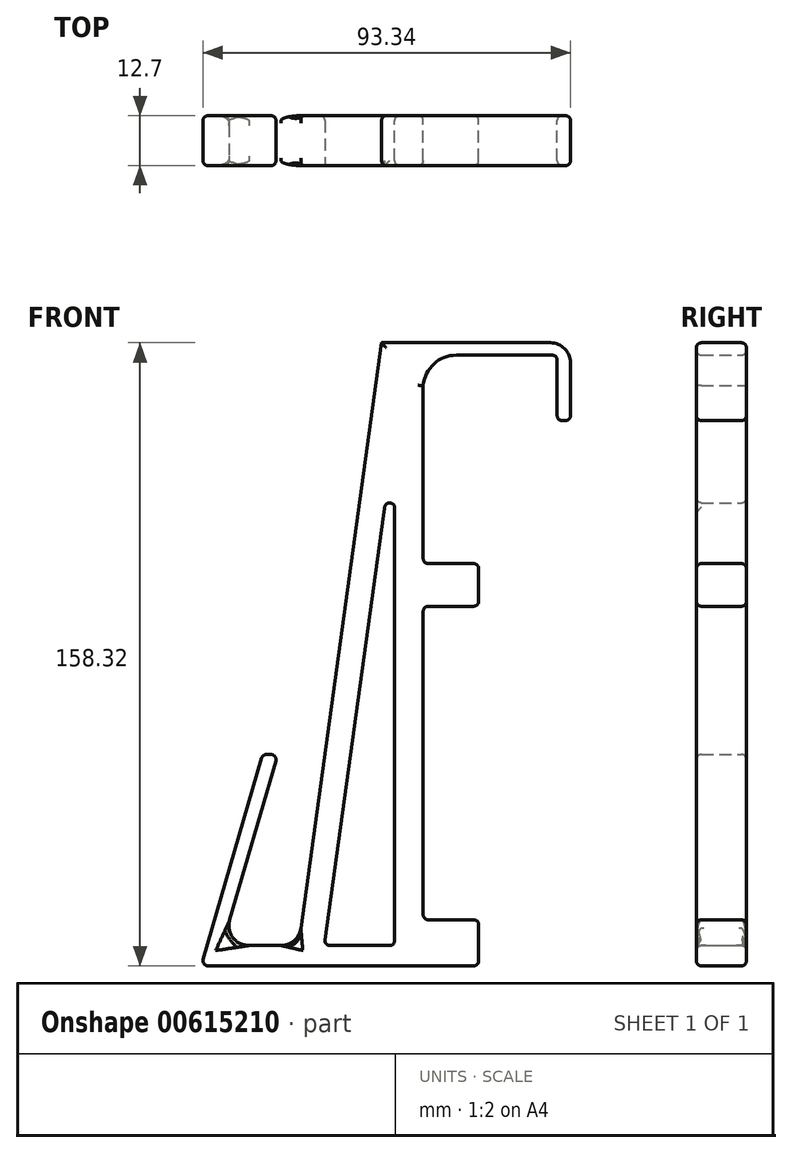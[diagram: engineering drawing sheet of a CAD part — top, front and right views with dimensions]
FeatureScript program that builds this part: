
annotation { "Feature Type Name" : "Feature", "Feature Type Description" : "" }
export const myFeature = defineFeature(function(context is Context, id is Id, definition is map)
    precondition{}
    {
        {
            var Q0;
            Q0=qCreatedBy(makeId("Front.planeOp"),FACE);
            var sketch = newSketch(context, id + "F0", { "sketchPlane" : qUnion([Q0])});
            skLineSegment(sketch, "E0", {"start": v(38.7, 133.36) * mm, "end": v(38.7, 150.01) * mm});
            skLineSegment(sketch, "E1", {"start": v(38.7, 150.01) * mm, "end": v(13.07, 150.01) * mm});
            skLineSegment(sketch, "E2", {"start": v(4.65, 142.3) * mm, "end": v(4.65, 97.04) * mm});
            skLineSegment(sketch, "E3", {"start": v(4.65, -5.16) * mm, "end": v(-51.7, -5.16) * mm});
            skLineSegment(sketch, "E4", {"start": v(-51.7, -5.16) * mm, "end": v(-36.14, 48.54) * mm});
            skLineSegment(sketch, "E5", {"start": v(-36.14, 48.54) * mm, "end": v(-32.33, 48.54) * mm});
            skLineSegment(sketch, "E6", {"start": v(-32.33, 48.54) * mm, "end": v(-46.39, 0) * mm});
            skLineSegment(sketch, "E7", {"start": v(-46.39, 0) * mm, "end": v(-27.04, 0) * mm});
            skLineSegment(sketch, "E8", {"start": v(-27.04, 0) * mm, "end": v(-6.11, 151.7) * mm});
            skLineSegment(sketch, "E9", {"start": v(-20.5, 0) * mm, "end": v(-2.6, 0) * mm});
            skPoint(sketch, "E10.start.orphan", {"position": v(0.23, 153.16) * mm});
            skLineSegment(sketch, "E11", {"start": v(-2.6, 129.72) * mm, "end": v(-20.5, 0) * mm});
            skLineSegment(sketch, "E12", {"start": v(4.65, 97.04) * mm, "end": v(18.75, 97.04) * mm});
            skLineSegment(sketch, "E13", {"start": v(18.75, 97.04) * mm, "end": v(18.75, 86.2) * mm});
            skLineSegment(sketch, "E14", {"start": v(18.75, 86.2) * mm, "end": v(4.65, 86.2) * mm});
            skLineSegment(sketch, "E15.trimOffspring", {"start": v(4.65, 86.2) * mm, "end": v(4.65, 6.56) * mm});
            skPoint(sketch, "E16.orphan", {"position": v(-5.91, 153.16) * mm});
            skLineSegment(sketch, "E17", {"start": v(4.65, 6.56) * mm, "end": v(18.75, 6.56) * mm});
            skLineSegment(sketch, "E18", {"start": v(18.75, 6.56) * mm, "end": v(18.75, -5.16) * mm});
            skLineSegment(sketch, "E19", {"start": v(18.75, -5.16) * mm, "end": v(4.65, -5.16) * mm});
            skLineSegment(sketch, "E20", {"start": v(38.7, 133.36) * mm, "end": v(42.06, 133.36) * mm});
            skLineSegment(sketch, "E21", {"start": v(42.06, 133.36) * mm, "end": v(42.06, 153.16) * mm});
            skLineSegment(sketch, "E22", {"start": v(42.06, 153.16) * mm, "end": v(-5.91, 153.16) * mm});
            skLineSegment(sketch, "E23", {"start": v(-6.11, 151.7) * mm, "end": v(-5.91, 153.16) * mm});
            skPoint(sketch, "E24.orphan", {"position": v(0, 129.72) * mm});
            skLineSegment(sketch, "E25", {"start": v(-2.6, 129.72) * mm, "end": v(-2.6, 0) * mm});
            skPoint(sketch, "E26.start.orphan", {"position": v(-1.3, 129.72) * mm});
            skPoint(sketch, "E27.centerSnap0", {"position": v(38.7, 141.69) * mm});
            skPoint(sketch, "E28", {"position": v(4.65, 142.3) * mm});
            skPoint(sketch, "E29", {"position": v(13.07, 150.01) * mm});
            skArc(sketch, "E30", {"start": v(13.07, 150.01) * mm, "mid": v(7.38, 147.77) * mm, "end": v(4.65, 142.3) * mm});
            skSolve(sketch);
        }
        {
            var Q0;
            Q0=makeQuery(id+"F0.imprint","IMPRINT",FACE,{"disambiguationData":[TD([[makeQuery(id+"F0.imprint","IMPRINT",EDGE,{"derivedFrom":sQuery(id+"F0.wireOp",EDGE,"KnBHMKyh-VmdD-H7sI-4YRO-vwrzje6zqPXn")}),-1.0]])]});
            var Q1;
            {var subQ2=sQuery(id+"F0.wireOp",EDGE,"E0");Q1=makeQuery(id+"F0.imprint","IMPRINT",FACE,{"disambiguationData":[TD([[makeQuery(id+"F0.imprint","IMPRINT",EDGE,{"derivedFrom":subQ2}),-1.0]])]});}
            extrude(context, id + "F1", {"entities" : qUnion([Q0, Q1]), "depth" : 12.7 * mm, "offsetDistance" : 25.4 * mm});
        }
        {
            var Q0;
            Q0=makeQuery(id+"F1.opExtrude","SWEPT_EDGE",EDGE,{"disambiguationData":[OSD([sQuery(id+"F0.wireOp",EDGE,"E11"),sQuery(id+"F0.wireOp",EDGE,"Bk6zNjHY-LAlG-lBTS-agNk-ghVCI7C8jAzF")])]});
            var Q1;
            Q1=makeQuery(id+"F1.opExtrude","CAP_EDGE",EDGE,{"disambiguationData":[OSD([sQuery(id+"F0.wireOp",EDGE,"Bk6zNjHY-LAlG-lBTS-agNk-ghVCI7C8jAzF")])],"isStart":false});
            var Q2;
            Q2=makeQuery(id+"F1.opExtrude","CAP_EDGE",EDGE,{"disambiguationData":[OSD([sQuery(id+"F0.wireOp",EDGE,"E26")])],"isStart":false});
            var Q3;
            Q3=makeQuery(id+"F1.opExtrude","SWEPT_EDGE",EDGE,{"disambiguationData":[OSD([sQuery(id+"F0.wireOp",EDGE,"Bk6zNjHY-LAlG-lBTS-agNk-ghVCI7C8jAzF"),sQuery(id+"F0.wireOp",EDGE,"E26")])]});
            var Q4;
            Q4=makeQuery(id+"F1.opExtrude","CAP_EDGE",EDGE,{"disambiguationData":[OSD([sQuery(id+"F0.wireOp",EDGE,"E25")])],"isStart":false});
            var Q5;
            Q5=makeQuery(id+"F1.opExtrude","CAP_EDGE",EDGE,{"disambiguationData":[OSD([sQuery(id+"F0.wireOp",EDGE,"E2")])],"isStart":false});
            var Q6;
            Q6=makeQuery(id+"F1.opExtrude","CAP_EDGE",EDGE,{"disambiguationData":[OSD([sQuery(id+"F0.wireOp",EDGE,"E2")])],"isStart":true});
            var Q7;
            Q7=makeQuery(id+"F1.opExtrude","CAP_EDGE",EDGE,{"disambiguationData":[OSD([sQuery(id+"F0.wireOp",EDGE,"E1")])],"isStart":false});
            var Q8;
            Q8=makeQuery(id+"F1.opExtrude","CAP_EDGE",EDGE,{"disambiguationData":[OSD([sQuery(id+"F0.wireOp",EDGE,"E21")])],"isStart":false});
            var Q9;
            Q9=makeQuery(id+"F1.opExtrude","CAP_EDGE",EDGE,{"disambiguationData":[OSD([sQuery(id+"F0.wireOp",EDGE,"E20")])],"isStart":false});
            var Q10;
            Q10=makeQuery(id+"F1.opExtrude","SWEPT_EDGE",EDGE,{"disambiguationData":[OSD([sQuery(id+"F0.wireOp",EDGE,"E20"),sQuery(id+"F0.wireOp",EDGE,"E21")])]});
            var Q11;
            Q11=makeQuery(id+"F1.opExtrude","SWEPT_EDGE",EDGE,{"disambiguationData":[OSD([sQuery(id+"F0.wireOp",EDGE,"E0"),sQuery(id+"F0.wireOp",EDGE,"E20")])]});
            var Q12;
            Q12=makeQuery(id+"F1.opExtrude","CAP_EDGE",EDGE,{"disambiguationData":[OSD([sQuery(id+"F0.wireOp",EDGE,"E1")])],"isStart":true});
            var Q13;
            Q13=makeQuery(id+"F1.opExtrude","CAP_EDGE",EDGE,{"disambiguationData":[OSD([sQuery(id+"F0.wireOp",EDGE,"E22")])],"isStart":false});
            var Q14;
            Q14=makeQuery(id+"F1.opExtrude","CAP_FACE",FACE,{"disambiguationData":[OSD([sQuery(id+"F0.wireOp",EDGE,"E0"),sQuery(id+"F0.wireOp",EDGE,"E1"),sQuery(id+"F0.wireOp",EDGE,"E2"),sQuery(id+"F0.wireOp",EDGE,"E3"),sQuery(id+"F0.wireOp",EDGE,"E4"),sQuery(id+"F0.wireOp",EDGE,"E5"),sQuery(id+"F0.wireOp",EDGE,"E6"),sQuery(id+"F0.wireOp",EDGE,"E7"),sQuery(id+"F0.wireOp",EDGE,"E8"),sQuery(id+"F0.wireOp",EDGE,"E9"),sQuery(id+"F0.wireOp",EDGE,"E11"),sQuery(id+"F0.wireOp",EDGE,"E12"),sQuery(id+"F0.wireOp",EDGE,"E13"),sQuery(id+"F0.wireOp",EDGE,"E14"),sQuery(id+"F0.wireOp",EDGE,"E15.trimOffspring"),sQuery(id+"F0.wireOp",EDGE,"E17"),sQuery(id+"F0.wireOp",EDGE,"E18"),sQuery(id+"F0.wireOp",EDGE,"E19"),sQuery(id+"F0.wireOp",EDGE,"E20"),sQuery(id+"F0.wireOp",EDGE,"E21"),sQuery(id+"F0.wireOp",EDGE,"E22"),sQuery(id+"F0.wireOp",EDGE,"E23"),sQuery(id+"F0.wireOp",EDGE,"E25")])],"isStart":true});
            var Q15;
            Q15=makeQuery(id+"F1.opExtrude","SWEPT_EDGE",EDGE,{"disambiguationData":[OSD([sQuery(id+"F0.wireOp",EDGE,"E4"),sQuery(id+"F0.wireOp",EDGE,"E5")])]});
            var Q16;
            Q16=makeQuery(id+"F1.opExtrude","SWEPT_EDGE",EDGE,{"disambiguationData":[OSD([sQuery(id+"F0.wireOp",EDGE,"E5"),sQuery(id+"F0.wireOp",EDGE,"E6")])]});
            var Q17;
            Q17=makeQuery(id+"F1.opExtrude","CAP_EDGE",EDGE,{"disambiguationData":[OSD([sQuery(id+"F0.wireOp",EDGE,"E5")])],"isStart":false});
            var Q18;
            Q18=makeQuery(id+"F1.opExtrude","CAP_EDGE",EDGE,{"disambiguationData":[OSD([sQuery(id+"F0.wireOp",EDGE,"E6")])],"isStart":false});
            var Q19;
            Q19=makeQuery(id+"F1.opExtrude","CAP_EDGE",EDGE,{"disambiguationData":[OSD([sQuery(id+"F0.wireOp",EDGE,"E4")])],"isStart":false});
            var Q20;
            Q20=makeQuery(id+"F1.opExtrude","CAP_EDGE",EDGE,{"disambiguationData":[OSD([sQuery(id+"F0.wireOp",EDGE,"E8"),sQuery(id+"F0.wireOp",EDGE,"E23")])],"isStart":false});
            var Q21;
            Q21=makeQuery(id+"F1.opExtrude","SWEPT_EDGE",EDGE,{"disambiguationData":[OSD([sQuery(id+"F0.wireOp",EDGE,"E12"),sQuery(id+"F0.wireOp",EDGE,"E13")])]});
            var Q22;
            Q22=makeQuery(id+"F1.opExtrude","SWEPT_EDGE",EDGE,{"disambiguationData":[OSD([sQuery(id+"F0.wireOp",EDGE,"E13"),sQuery(id+"F0.wireOp",EDGE,"E14")])]});
            var Q23;
            Q23=makeQuery(id+"F1.opExtrude","CAP_EDGE",EDGE,{"disambiguationData":[OSD([sQuery(id+"F0.wireOp",EDGE,"E13")])],"isStart":false});
            var Q24;
            Q24=makeQuery(id+"F1.opExtrude","CAP_EDGE",EDGE,{"disambiguationData":[OSD([sQuery(id+"F0.wireOp",EDGE,"E12")])],"isStart":false});
            var Q25;
            Q25=makeQuery(id+"F1.opExtrude","CAP_EDGE",EDGE,{"disambiguationData":[OSD([sQuery(id+"F0.wireOp",EDGE,"E14")])],"isStart":false});
            var Q26;
            Q26=makeQuery(id+"F1.opExtrude","CAP_EDGE",EDGE,{"disambiguationData":[OSD([sQuery(id+"F0.wireOp",EDGE,"E15.trimOffspring")])],"isStart":false});
            var Q27;
            Q27=makeQuery(id+"F1.opExtrude","CAP_EDGE",EDGE,{"disambiguationData":[OSD([sQuery(id+"F0.wireOp",EDGE,"E0")])],"isStart":false});
            var Q28;
            Q28=makeQuery(id+"F1.opExtrude","SWEPT_EDGE",EDGE,{"disambiguationData":[OSD([sQuery(id+"F0.wireOp",EDGE,"E9"),sQuery(id+"F0.wireOp",EDGE,"E25")])]});
            var Q29;
            Q29=makeQuery(id+"F1.opExtrude","SWEPT_EDGE",EDGE,{"disambiguationData":[OSD([sQuery(id+"F0.wireOp",EDGE,"E3"),sQuery(id+"F0.wireOp",EDGE,"E4")])]});
            var Q30;
            Q30=makeQuery(id+"F1.opExtrude","CAP_EDGE",EDGE,{"disambiguationData":[OSD([sQuery(id+"F0.wireOp",EDGE,"E17")])],"isStart":false});
            var Q31;
            Q31=makeQuery(id+"F1.opExtrude","CAP_EDGE",EDGE,{"disambiguationData":[OSD([sQuery(id+"F0.wireOp",EDGE,"E18")])],"isStart":false});
            var Q32;
            Q32=makeQuery(id+"F1.opExtrude","CAP_EDGE",EDGE,{"disambiguationData":[OSD([sQuery(id+"F0.wireOp",EDGE,"E3"),sQuery(id+"F0.wireOp",EDGE,"E19")])],"isStart":false});
            var Q33;
            Q33=makeQuery(id+"F1.opExtrude","SWEPT_EDGE",EDGE,{"disambiguationData":[OSD([sQuery(id+"F0.wireOp",EDGE,"E17"),sQuery(id+"F0.wireOp",EDGE,"E18")])]});
            var Q34;
            Q34=makeQuery(id+"F1.opExtrude","SWEPT_EDGE",EDGE,{"disambiguationData":[OSD([sQuery(id+"F0.wireOp",EDGE,"E15.trimOffspring"),sQuery(id+"F0.wireOp",EDGE,"E17")])]});
            var Q35;
            Q35=makeQuery(id+"F1.opExtrude","SWEPT_EDGE",EDGE,{"disambiguationData":[OSD([sQuery(id+"F0.wireOp",EDGE,"E18"),sQuery(id+"F0.wireOp",EDGE,"E19")])]});
            var Q36;
            Q36=makeQuery(id+"F1.opExtrude","SWEPT_EDGE",EDGE,{"disambiguationData":[OSD([sQuery(id+"F0.wireOp",EDGE,"E0"),sQuery(id+"F0.wireOp",EDGE,"E1")])]});
            var Q37;
            Q37=makeQuery(id+"F1.opExtrude","CAP_EDGE",EDGE,{"disambiguationData":[OSD([sQuery(id+"F0.wireOp",EDGE,"E7")])],"isStart":false});
            var Q38;
            Q38=makeQuery(id+"F1.opExtrude","SWEPT_EDGE",EDGE,{"disambiguationData":[OSD([sQuery(id+"F0.wireOp",EDGE,"E2"),sQuery(id+"F0.wireOp",EDGE,"E12")])]});
            var Q39;
            Q39=makeQuery(id+"F1.opExtrude","SWEPT_EDGE",EDGE,{"disambiguationData":[OSD([sQuery(id+"F0.wireOp",EDGE,"E14"),sQuery(id+"F0.wireOp",EDGE,"E15.trimOffspring")])]});
            fillet(context, id + "F2", {"entities" : qUnion([Q0, Q1, Q2, Q3, Q4, Q5, Q6, Q7, Q8, Q9, Q10, Q11, Q12, Q13, Q14, Q15, Q16, Q17, Q18, Q19, Q20, Q21, Q22, Q23, Q24, Q25, Q26, Q27, Q28, Q29, Q30, Q31, Q32, Q33, Q34, Q35, Q36, Q37, Q38, Q39]), "radius" : 1.27 * mm, "tangentPropagation" : true, "allowEdgeOverflow" : false});
        }
        {
            var Q0;
            Q0=makeQuery(id+"F1.opExtrude","SWEPT_EDGE",EDGE,{"disambiguationData":[OSD([sQuery(id+"F0.wireOp",EDGE,"E21"),sQuery(id+"F0.wireOp",EDGE,"E22")])]});
            var Q1;
            Q1=makeQuery(id+"F1.opExtrude","SWEPT_EDGE",EDGE,{"disambiguationData":[OSD([sQuery(id+"F0.wireOp",EDGE,"E6"),sQuery(id+"F0.wireOp",EDGE,"E7")])]});
            var Q2;
            Q2=makeQuery(id+"F1.opExtrude","SWEPT_EDGE",EDGE,{"disambiguationData":[OSD([sQuery(id+"F0.wireOp",EDGE,"E7"),sQuery(id+"F0.wireOp",EDGE,"E8")])]});
            fillet(context, id + "F3", {"entities" : qUnion([Q0, Q1, Q2]), "radius" : 5.08 * mm, "tangentPropagation" : true, "allowEdgeOverflow" : false});
        }
    });
